# Revit family: QF_BOURGEAT_3GN_bain_marie mobile_sans_etuve_cuve_simple
name_source: partatom
category: Equipement spécialisé
revit_build: Autodesk Revit 2015 (Build: 20140606_1530(x64)
units: mm (PartAtom-declared; Revit-internal decimal feet)

## types (1)
- 3GN_bain_marie_cuve_simple
    Charge max = 90.00 kg
    Diamètre de Raccordement Evacuation = 27 mm
    Fabricant = BOURGEAT
    Fréquence = 50 Hz
    Hauteur hors tout = 900 mm  [stored 2.95276 ft]
    Indice de protection = 33
    Intensité nominale = 6 A
    Longueur hors tout = 1280 mm  [stored 4.19948 ft]
    Modèle = 872003
    Nature isolant = 30mm laine de roche
    Phase = 2
    Poids net à vide = 55.00 kg
    Profondeur hors tout = 690 mm  [stored 2.26378 ft]
    Puissance électrique  = 2100 W
    Spécification du Fabricant = bain-marie mobiles
    Tension = 230 V
    URL Fabricant = http://www.bourgeat.fr

note: [stored X ft] marks values corroborated as IEEE doubles in the binary element streams (Revit-internal decimal feet)
